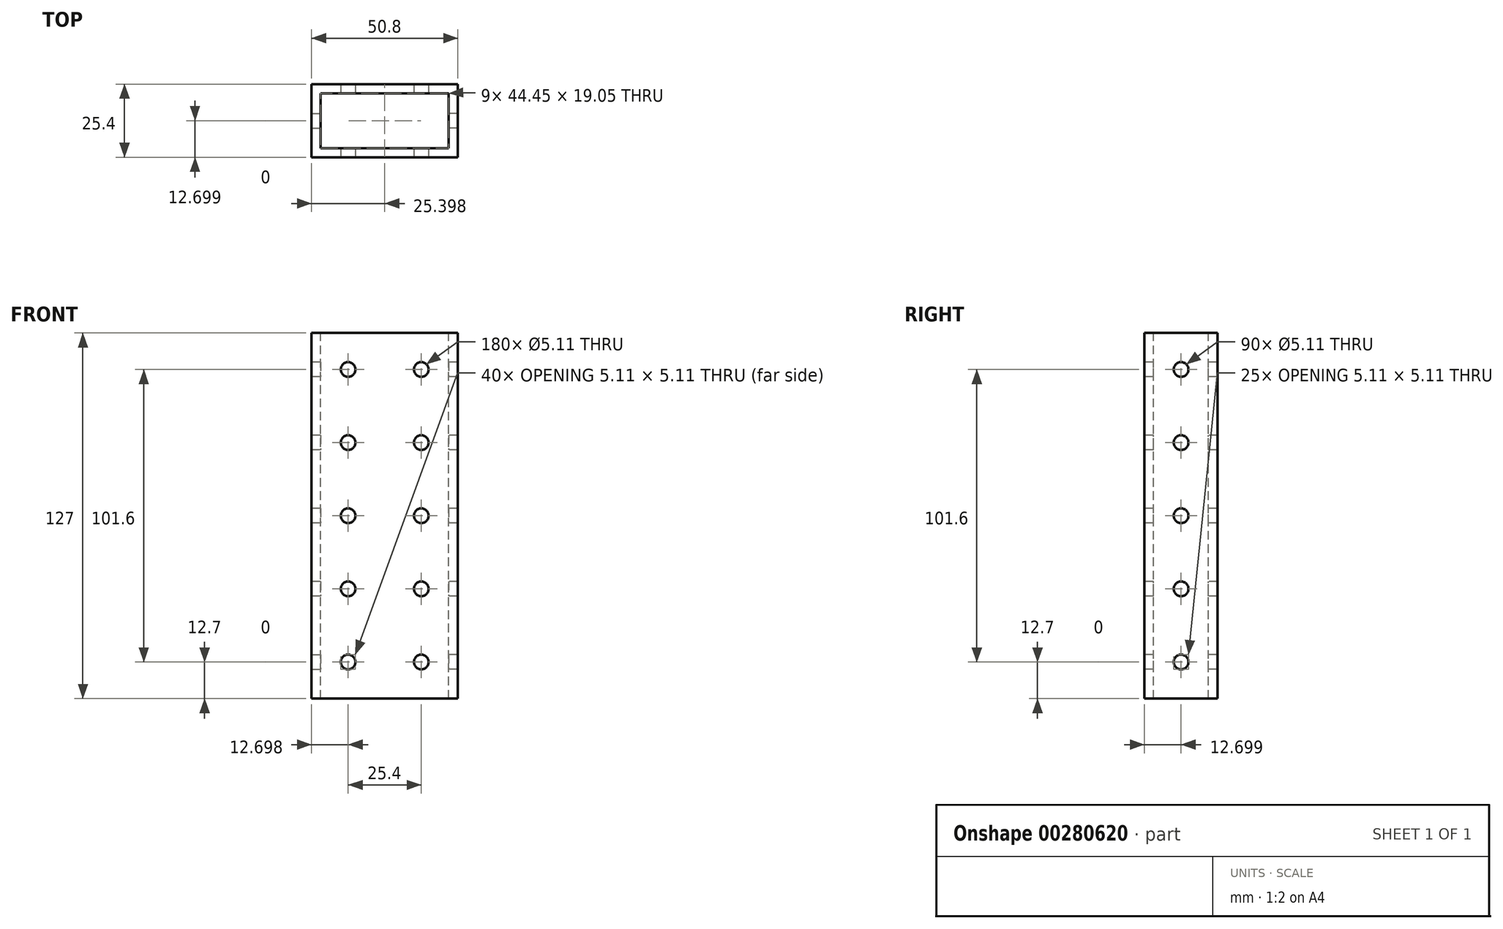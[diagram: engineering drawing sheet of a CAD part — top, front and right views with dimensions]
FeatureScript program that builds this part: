
annotation { "Feature Type Name" : "Feature", "Feature Type Description" : "" }
export const myFeature = defineFeature(function(context is Context, id is Id, definition is map)
    precondition{}
    {
        {
            var Q0;
            Q0=qCreatedBy(makeId("Top.planeOp"),FACE);
            var sketch = newSketch(context, id + "F0", { "sketchPlane" : qUnion([Q0])});
            skLineSegment(sketch, "E0.bottom", {"start": v(-19.05, 5.92) * mm, "end": v(31.75, 5.92) * mm});
            skLineSegment(sketch, "E0.top", {"start": v(-19.05, -19.48) * mm, "end": v(31.75, -19.48) * mm});
            skLineSegment(sketch, "E0.left", {"start": v(-19.05, 5.92) * mm, "end": v(-19.05, -19.48) * mm});
            skLineSegment(sketch, "E0.right", {"start": v(31.75, 5.92) * mm, "end": v(31.75, -19.48) * mm});
            skSolve(sketch);
        }
        {
            var Q0;
            Q0 = qSketchRegion(id + "F0", true);
            extrude(context, id + "F1", {"entities" : qUnion([Q0]), "depth" : 127 * mm});
        }
        {
            var Q0;
            Q0=makeQuery(id+"F1.opExtrude","CAP_FACE",FACE,{"disambiguationData":[OSD([sQuery(id+"F0.wireOp",EDGE,"E0.bottom"),sQuery(id+"F0.wireOp",EDGE,"E0.top"),sQuery(id+"F0.wireOp",EDGE,"E0.left"),sQuery(id+"F0.wireOp",EDGE,"E0.right")])],"isStart":false});
            var sketch = newSketch(context, id + "F2", { "sketchPlane" : qUnion([Q0])});
            skLineSegment(sketch, "E1.bottom", {"start": v(-15.88, 2.74) * mm, "end": v(28.57, 2.74) * mm});
            skLineSegment(sketch, "E1.top", {"start": v(-15.88, -16.3) * mm, "end": v(28.57, -16.3) * mm});
            skLineSegment(sketch, "E1.left", {"start": v(-15.88, 2.74) * mm, "end": v(-15.88, -16.3) * mm});
            skLineSegment(sketch, "E1.right", {"start": v(28.57, 2.74) * mm, "end": v(28.57, -16.3) * mm});
            skSolve(sketch);
        }
        {
            var Q0;
            Q0=makeQuery(id+"F2.imprint","IMPRINT",FACE,{"disambiguationData":[TD([[makeQuery(id+"F2.imprint","IMPRINT",EDGE,{"derivedFrom":sQuery(id+"F2.wireOp",EDGE,"E1.bottom")}),-1.0]])]});
            extrude(context, id + "F3", {"entities" : qUnion([Q0]), "operationType" : NewBodyOperationType.REMOVE, "oppositeDirection" : true, "depth" : 127 * mm});
        }
        {
            var Q0;
            Q0=qCreatedBy(makeId("Right.planeOp"),FACE);
            var sketch = newSketch(context, id + "F4", { "sketchPlane" : qUnion([Q0])});
            skCircle(sketch, "E2", {"center": v(-6.78, 12.7) * mm, "radius": 2.55 * mm});
            skSolve(sketch);
        }
        {
            var Q0;
            Q0=sQuery(id+"F4.wireOp",VERTEX,"E2.center");
            var Q1;
            Q1=makeQuery(id+"F1.opExtrude","SWEPT_BODY",BODY,{"disambiguationData":[OSD([sQuery(id+"F0.wireOp",EDGE,"E0.bottom"),sQuery(id+"F0.wireOp",EDGE,"E0.top"),sQuery(id+"F0.wireOp",EDGE,"E0.left"),sQuery(id+"F0.wireOp",EDGE,"E0.right")])]});
            hole(context, id + "F5", {"style" : HoleStyle.SIMPLE, "endStyle" : HoleEndStyle.THROUGH, "holeDiameter" : 5.1 * mm, "tappedDepth" : 12.7 * mm, "tapClearance" : 3, "locations" : qUnion([Q0]), "scope" : qUnion([Q1])});
        }
        {
            var Q0;
            Q0=makeQuery(id+"F1.opExtrude","SWEPT_FACE",FACE,{"disambiguationData":[OSD([sQuery(id+"F0.wireOp",EDGE,"E0.top")])]});
            var sketch = newSketch(context, id + "F6", { "sketchPlane" : qUnion([Q0])});
            skCircle(sketch, "E3", {"center": v(-6.35, 114.3) * mm, "radius": 2.55 * mm});
            skCircle(sketch, "E4.0.1.0", {"center": v(-6.35, 88.9) * mm, "radius": 2.55 * mm});
            skCircle(sketch, "E4.0.2.0", {"center": v(-6.35, 63.5) * mm, "radius": 2.55 * mm});
            skCircle(sketch, "E4.0.3.0", {"center": v(-6.35, 38.1) * mm, "radius": 2.55 * mm});
            skCircle(sketch, "E4.0.4.0", {"center": v(-6.35, 12.7) * mm, "radius": 2.55 * mm});
            skCircle(sketch, "E4.1.0.0", {"center": v(19.05, 114.3) * mm, "radius": 2.55 * mm});
            skCircle(sketch, "E4.1.1.0", {"center": v(19.05, 88.9) * mm, "radius": 2.55 * mm});
            skCircle(sketch, "E4.1.2.0", {"center": v(19.05, 63.5) * mm, "radius": 2.55 * mm});
            skCircle(sketch, "E4.1.3.0", {"center": v(19.05, 38.1) * mm, "radius": 2.55 * mm});
            skCircle(sketch, "E4.1.4.0", {"center": v(19.05, 12.7) * mm, "radius": 2.55 * mm});
            skLineSegment(sketch, "E4.direction1", {"start": v(-6.35, 114.3) * mm, "end": v(19.05, 114.3) * mm, "construction": true});
            skLineSegment(sketch, "E4.direction2", {"start": v(-6.35, 114.3) * mm, "end": v(-6.35, 88.9) * mm, "construction": true});
            skSolve(sketch);
        }
        {
            var Q0;
            Q0=sQuery(id+"F6.wireOp",VERTEX,"E4.1.4.0.center");
            var Q1;
            Q1=sQuery(id+"F6.wireOp",VERTEX,"E4.0.1.0.center");
            var Q2;
            Q2=sQuery(id+"F6.wireOp",VERTEX,"E4.0.2.0.center");
            var Q3;
            Q3=sQuery(id+"F6.wireOp",VERTEX,"E4.0.3.0.center");
            var Q4;
            Q4=sQuery(id+"F6.wireOp",VERTEX,"E4.1.1.0.center");
            var Q5;
            Q5=sQuery(id+"F6.wireOp",VERTEX,"E4.1.0.0.center");
            var Q6;
            Q6=sQuery(id+"F6.wireOp",VERTEX,"E4.0.4.0.center");
            var Q7;
            Q7=sQuery(id+"F6.wireOp",VERTEX,"E4.direction1.start");
            var Q8;
            Q8=sQuery(id+"F6.wireOp",VERTEX,"E4.1.3.0.center");
            var Q9;
            Q9=sQuery(id+"F6.wireOp",VERTEX,"E4.1.2.0.center");
            var Q10;
            Q10=makeQuery(id+"F1.opExtrude","SWEPT_BODY",BODY,{"disambiguationData":[OSD([sQuery(id+"F0.wireOp",EDGE,"E0.bottom"),sQuery(id+"F0.wireOp",EDGE,"E0.top"),sQuery(id+"F0.wireOp",EDGE,"E0.left"),sQuery(id+"F0.wireOp",EDGE,"E0.right")])]});
            hole(context, id + "F7", {"style" : HoleStyle.SIMPLE, "endStyle" : HoleEndStyle.THROUGH, "holeDiameter" : 5.1 * mm, "tappedDepth" : 12.7 * mm, "tapClearance" : 3, "locations" : qUnion([Q0, Q1, Q2, Q3, Q4, Q5, Q6, Q7, Q8, Q9]), "scope" : qUnion([Q10])});
        }
        {
            var Q0;
            Q0=makeQuery(id+"F1.opExtrude","SWEPT_FACE",FACE,{"disambiguationData":[OSD([sQuery(id+"F0.wireOp",EDGE,"E0.left")])]});
            var sketch = newSketch(context, id + "F8", { "sketchPlane" : qUnion([Q0])});
            skCircle(sketch, "E5", {"center": v(6.78, 114.3) * mm, "radius": 2.55 * mm});
            skCircle(sketch, "E6.0.1.0", {"center": v(6.78, 88.9) * mm, "radius": 2.55 * mm});
            skCircle(sketch, "E6.0.2.0", {"center": v(6.78, 63.5) * mm, "radius": 2.55 * mm});
            skCircle(sketch, "E6.0.3.0", {"center": v(6.78, 38.1) * mm, "radius": 2.55 * mm});
            skCircle(sketch, "E6.0.4.0", {"center": v(6.78, 12.7) * mm, "radius": 2.55 * mm});
            skLineSegment(sketch, "E6.direction1", {"start": v(6.78, 114.3) * mm, "end": v(32.18, 114.3) * mm, "construction": true});
            skLineSegment(sketch, "E6.direction2", {"start": v(6.78, 114.3) * mm, "end": v(6.78, 88.9) * mm, "construction": true});
            skSolve(sketch);
        }
        {
            var Q0;
            Q0=sQuery(id+"F8.wireOp",VERTEX,"E6.0.1.0.center");
            var Q1;
            Q1=sQuery(id+"F8.wireOp",VERTEX,"E5.center");
            var Q2;
            Q2=sQuery(id+"F8.wireOp",VERTEX,"E6.0.2.0.center");
            var Q3;
            Q3=sQuery(id+"F8.wireOp",VERTEX,"E6.0.4.0.center");
            var Q4;
            Q4=sQuery(id+"F8.wireOp",VERTEX,"E6.0.3.0.center");
            var Q5;
            Q5=makeQuery(id+"F1.opExtrude","SWEPT_BODY",BODY,{"disambiguationData":[OSD([sQuery(id+"F0.wireOp",EDGE,"E0.bottom"),sQuery(id+"F0.wireOp",EDGE,"E0.top"),sQuery(id+"F0.wireOp",EDGE,"E0.left"),sQuery(id+"F0.wireOp",EDGE,"E0.right")])]});
            hole(context, id + "F9", {"style" : HoleStyle.SIMPLE, "endStyle" : HoleEndStyle.THROUGH, "holeDiameter" : 5.1 * mm, "tappedDepth" : 12.7 * mm, "tapClearance" : 3, "locations" : qUnion([Q0, Q1, Q2, Q3, Q4]), "scope" : qUnion([Q5])});
        }
    });
